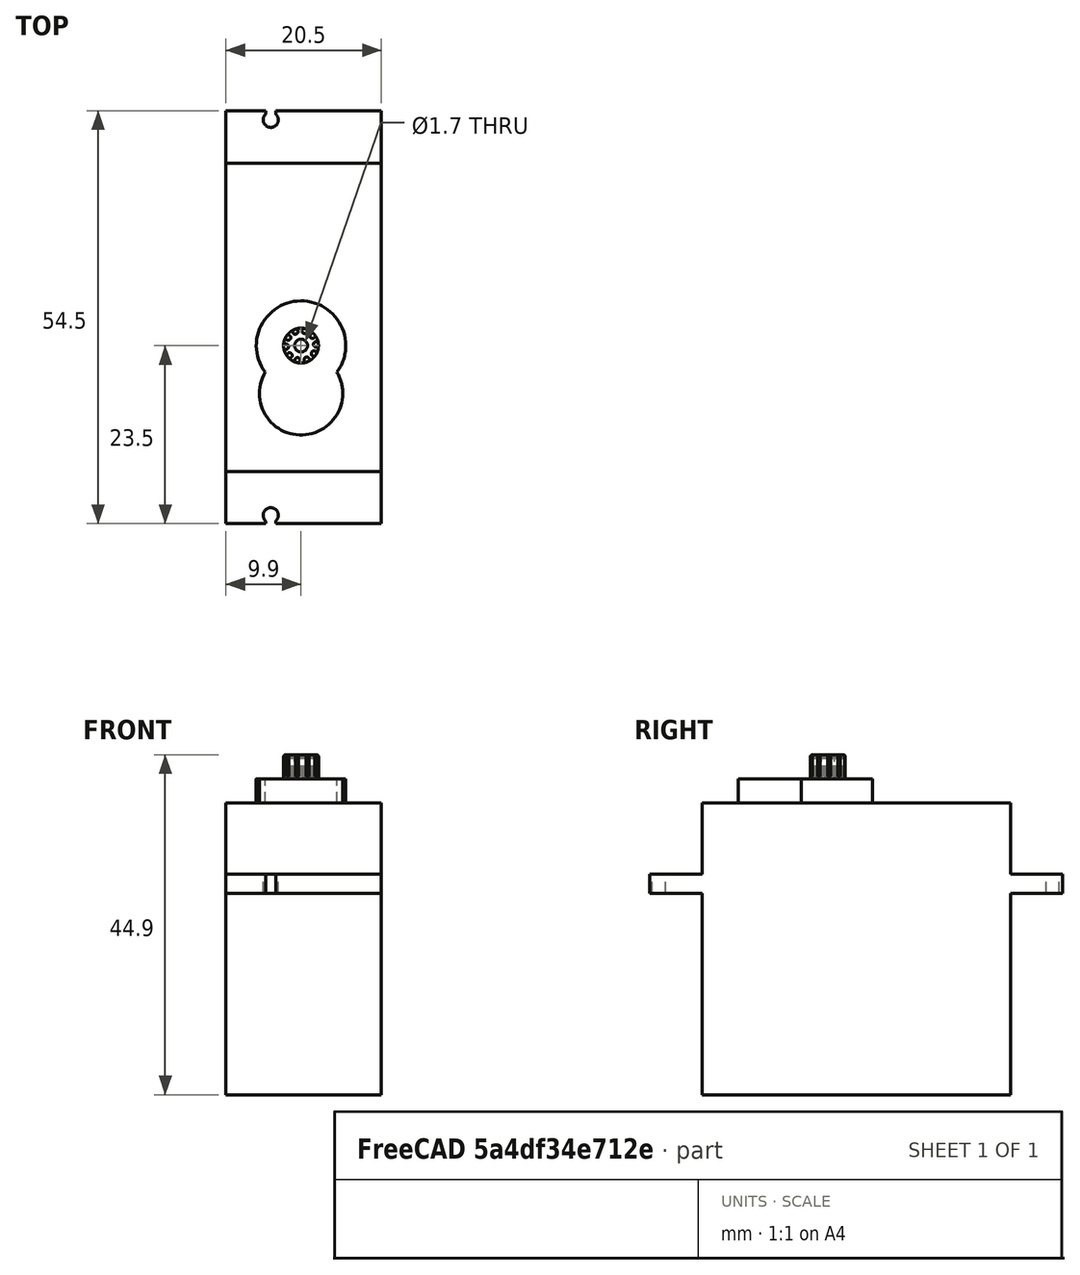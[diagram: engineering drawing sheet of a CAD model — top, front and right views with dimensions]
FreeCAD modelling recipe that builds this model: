
FCSTD DOCUMENT  (FreeCAD 0.19R24267 +99 (Git))
Label: Servo TGY-WP23
License: CreativeCommons Attribution-ShareAlike
LicenseURL: http://creativecommons.org/licenses/by-sa/4.0/
objects: Part::Cylinder×7, Part::Fuse×6, Part::Box×4, Part::Cut×3, Part::FeaturePython×1, Part::Fillet×1, App::DocumentObjectGroup×1, Part::Compound×1
note: 23 computed .brp shape members not serialized (recipe doc carries the construction recipe); baked Part::Feature solids carry a one-line shape summary decoded from their .brp

FEATURE [Part::Box] Box  label="Cubo"
  AttacherType = Attacher::AttachEngine3D
  Height = 38.5
  Length = 20.5
  Width = 40.7
FEATURE [Part::Box] Box001  label="Cubo001"
  AttacherType = Attacher::AttachEngine3D
  Height = 2.5
  Length = 20.5
  Placement = pos=(0,-6.9,26.6) rot=(0,0,1;0rad)
  Width = 54.5
FEATURE [Part::Fuse] Fusion  label="Square_body"
  Base = -> Box
  Refine = true
  Tool = -> Box001
FEATURE [Part::Cylinder] Cylinder  label="Cilindro"
  Angle = 360
  AttacherType = Attacher::AttachEngine3D
  Height = 4
  Placement = pos=(9.9,16.6,37.7) rot=(0,0,1;0rad)
  Radius = 5.9
FEATURE [Part::Cylinder] Cylinder001  label="Cilindro001"
  Angle = 360
  AttacherType = Attacher::AttachEngine3D
  Height = 4
  Placement = pos=(9.9,10.3,37.7) rot=(0,0,1;0rad)
  Radius = 5.5
FEATURE [Part::Fuse] Fusion001
  Base = -> Cylinder
  Refine = true
  Tool = -> Cylinder001
FEATURE [Part::Fuse] Fusion003
  Base = -> Fusion
  Refine = true
  Tool = -> Fusion001
FEATURE [Part::Cylinder] Cylinder003  label="Taladro"
  Angle = 360
  AttacherType = Attacher::AttachEngine3D
  Height = 10
  Placement = pos=(5.9,-5.8,21) rot=(0,0,1;0rad)
  Radius = 1
FEATURE [Part::Cylinder] Cylinder004  label="Taladro2"
  Angle = 360
  AttacherType = Attacher::AttachEngine3D
  Height = 10
  Placement = pos=(5.9,46.4,21) rot=(0,0,1;0rad)
  Radius = 1
FEATURE [Part::Fuse] Fusion004  label="Taladros"
  Base = -> Cylinder003
  Refine = true
  Tool = -> Cylinder004
FEATURE [Part::Box] Box002  label="Cubo002"
  AttacherType = Attacher::AttachEngine3D
  Height = 10
  Length = 1.3
  Placement = pos=(5.25,-9,20) rot=(0,0,1;0rad)
  Width = 3.3
FEATURE [Part::Box] Box003  label="Cubo003"
  AttacherType = Attacher::AttachEngine3D
  Height = 10
  Length = 1.3
  Placement = pos=(5.25,46,20) rot=(0,0,1;0rad)
  Width = 3.3
FEATURE [Part::Fuse] Fusion005  label="Rebajes"
  Base = -> Box002
  Refine = true
  Tool = -> Box003
FEATURE [Part::Fuse] Fusion006  label="Taladros001"
  Base = -> Fusion004
  Refine = true
  Tool = -> Fusion005
FEATURE [Part::Cut] Cut  label="Cuerpo_con_taladros"
  Base = -> Fusion003
  Placement = pos=(-5.9,0,0) rot=(0,0,1;0rad)
  Refine = true
  Tool = -> Fusion006
FEATURE [Part::Cylinder] Cylinder006  label="Cilindro002"
  Angle = 360
  AttacherType = Attacher::AttachEngine3D
  Height = 3
  Placement = pos=(1.7,15.55,42) rot=(0,0,1;0rad)
  Radius = 0.35
FEATURE [Part::FeaturePython] Array  # Draft array (typed FeaturePython)
  Angle = 360
  ArrayType = 1
  Axis = (0,0,1)
  Base = -> Cylinder006
  Center = (0,16.6,0)
  Fuse = false
  IntervalAxis = (0,0,0)
  IntervalX = (1,0,0)
  IntervalY = (0,1,0)
  IntervalZ = (0,0,0)
  NumberPolar = 20
  NumberX = 2
  NumberY = 2
  NumberZ = 1
  Placement = pos=(4,0,0) rot=(0,0,1;0rad)
FEATURE [Part::Cylinder] Cylinder002  label="Cilindro_interior"
  Angle = 360
  AttacherType = Attacher::AttachEngine3D
  Height = 3.2
  Placement = pos=(4,16.6,41.7) rot=(0,0,1;0rad)
  Radius = 2.3
FEATURE [Part::Cylinder] Cylinder005  label="Cilindro_exterior"
  Angle = 360
  AttacherType = Attacher::AttachEngine3D
  Height = 3.2
  Placement = pos=(4,16.6,41.7) rot=(0,0,1;0rad)
  Radius = 0.85
FEATURE [Part::Cut] Cut001  label="Cilindro_vaciado"
  Base = -> Cylinder002
  Refine = true
  Tool = -> Cylinder005
FEATURE [Part::Fillet] Fillet
  Base = -> Cut001
  Edges = 1 edges r=0.3: [Edge1]
FEATURE [Part::Cut] Cut002  label="Eje_engranaje"
  Base = -> Fillet
  Refine = true
  Tool = -> Array
FEATURE [App::DocumentObjectGroup] Grupo003  label="Servo"
  Group = -> [Cut,Cut002]
FEATURE [Part::Compound] Compound
  Links = -> [Cut,Cut002]
